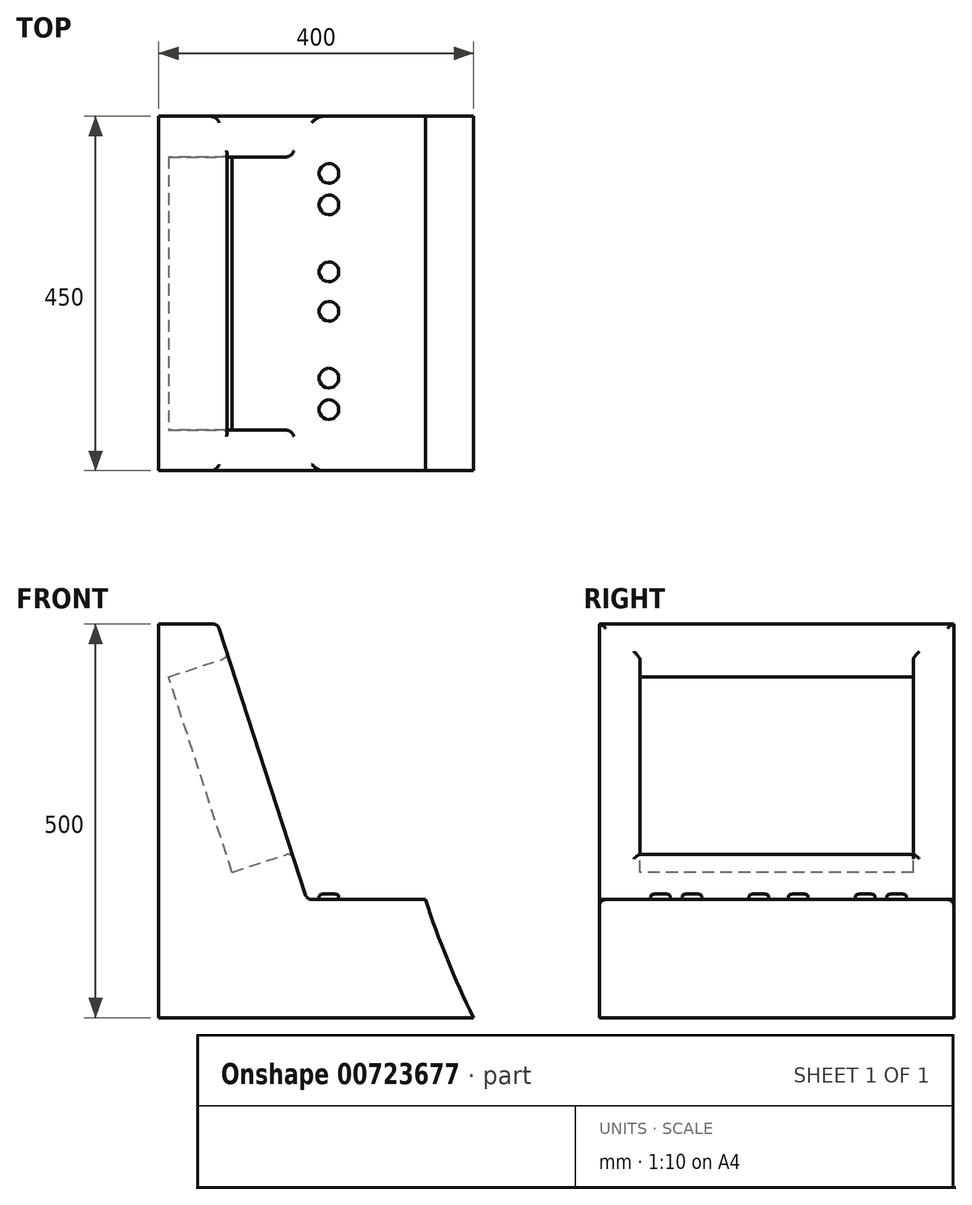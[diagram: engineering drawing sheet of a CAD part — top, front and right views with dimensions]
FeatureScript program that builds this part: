
annotation { "Feature Type Name" : "Feature", "Feature Type Description" : "" }
export const myFeature = defineFeature(function(context is Context, id is Id, definition is map)
    precondition{}
    {
        {
            var Q0;
            Q0=qCreatedBy(makeId("Front.planeOp"),FACE);
            var sketch = newSketch(context, id + "F0", { "sketchPlane" : qUnion([Q0])});
            skLineSegment(sketch, "E0", {"start": v(-195.47, 342.68) * mm, "end": v(-195.47, -157.32) * mm});
            skLineSegment(sketch, "E1", {"start": v(204.53, -157.32) * mm, "end": v(-195.47, -157.32) * mm});
            skLineSegment(sketch, "E2", {"start": v(143.25, -7.32) * mm, "end": v(-6.75, -7.32) * mm});
            skLineSegment(sketch, "E3", {"start": v(-195.47, 342.68) * mm, "end": v(-120.47, 342.68) * mm});
            skLineSegment(sketch, "E4", {"start": v(-120.47, 342.68) * mm, "end": v(-6.75, -7.32) * mm});
            skArc(sketch, "E5", {"start": v(143.25, -7.32) * mm, "mid": v(171.35, -83.36) * mm, "end": v(204.53, -157.32) * mm});
            skSolve(sketch);
        }
        {
            var Q0;
            Q0=makeQuery(id+"F0.imprint","IMPRINT",FACE,{"disambiguationData":[TD([[makeQuery(id+"F0.imprint","IMPRINT",EDGE,{"derivedFrom":sQuery(id+"F0.wireOp",EDGE,"E0")}),1.0]])]});
            extrude(context, id + "F1", {"entities" : qUnion([Q0]), "depth" : 450 * mm, "offsetDistance" : 25 * mm});
        }
        {
            var Q0;
            Q0=makeQuery(id+"F1.opExtrude","SWEPT_FACE",FACE,{"disambiguationData":[OSD([sQuery(id+"F0.wireOp",EDGE,"E4")])]});
            var sketch = newSketch(context, id + "F2", { "sketchPlane" : qUnion([Q0])});
            skLineSegment(sketch, "E6.bottom", {"start": v(-51.5, 57.64) * mm, "end": v(-398.5, 57.64) * mm});
            skLineSegment(sketch, "E6.top", {"start": v(-51.5, 318.64) * mm, "end": v(-398.5, 318.64) * mm});
            skLineSegment(sketch, "E6.left", {"start": v(-51.5, 57.64) * mm, "end": v(-51.5, 318.64) * mm});
            skLineSegment(sketch, "E6.right", {"start": v(-398.5, 57.64) * mm, "end": v(-398.5, 318.64) * mm});
            skPoint(sketch, "E6.middle", {"position": v(-225, 188.14) * mm});
            skSolve(sketch);
        }
        {
            var Q0;
            Q0=makeQuery(id+"F2.imprint","IMPRINT",FACE,{"disambiguationData":[TD([[makeQuery(id+"F2.imprint","IMPRINT",EDGE,{"derivedFrom":sQuery(id+"F2.wireOp",EDGE,"E6.bottom")}),-1.0]])]});
            extrude(context, id + "F3", {"entities" : qUnion([Q0]), "operationType" : NewBodyOperationType.REMOVE, "oppositeDirection" : true, "depth" : 80 * mm, "offsetDistance" : 25 * mm});
        }
        {
            var Q0;
            Q0=makeQuery(id+"F1.opExtrude","SWEPT_FACE",FACE,{"disambiguationData":[OSD([sQuery(id+"F0.wireOp",EDGE,"E4")])]});
            fillet(context, id + "F4", {"entities" : qUnion([Q0]), "radius" : 8 * mm, "tangentPropagation" : true, "allowEdgeOverflow" : false});
        }
        {
            var Q0;
            Q0=makeQuery(id+"F1.opExtrude","SWEPT_FACE",FACE,{"disambiguationData":[OSD([sQuery(id+"F0.wireOp",EDGE,"E2")])]});
            var sketch = newSketch(context, id + "F5", { "sketchPlane" : qUnion([Q0])});
            skLineSegment(sketch, "E7", {"start": v(20.89, -442) * mm, "end": v(20.89, -8) * mm, "construction": true});
            skCircle(sketch, "E8", {"center": v(20.89, -372.5) * mm, "radius": 12.5 * mm});
            skCircle(sketch, "E9", {"center": v(20.89, -332.5) * mm, "radius": 12.5 * mm});
            skCircle(sketch, "E10", {"center": v(20.89, -247.5) * mm, "radius": 12.5 * mm});
            skCircle(sketch, "E11", {"center": v(20.89, -197.5) * mm, "radius": 12.5 * mm});
            skCircle(sketch, "E12", {"center": v(20.89, -112.5) * mm, "radius": 12.5 * mm});
            skCircle(sketch, "E13", {"center": v(20.89, -72.5) * mm, "radius": 12.5 * mm});
            skSolve(sketch);
        }
        {
            var Q0;
            Q0=makeQuery(id+"F5.imprint","IMPRINT",FACE,{"disambiguationData":[TD([[makeQuery(id+"F5.imprint","IMPRINT",EDGE,{"derivedFrom":sQuery(id+"F5.wireOp",EDGE,"E8")}),1.0]])]});
            var Q1;
            Q1=makeQuery(id+"F5.imprint","IMPRINT",FACE,{"disambiguationData":[TD([[makeQuery(id+"F5.imprint","IMPRINT",EDGE,{"derivedFrom":sQuery(id+"F5.wireOp",EDGE,"E9")}),1.0]])]});
            var Q2;
            Q2=makeQuery(id+"F5.imprint","IMPRINT",FACE,{"disambiguationData":[TD([[makeQuery(id+"F5.imprint","IMPRINT",EDGE,{"derivedFrom":sQuery(id+"F5.wireOp",EDGE,"E10")}),1.0]])]});
            var Q3;
            Q3=makeQuery(id+"F5.imprint","IMPRINT",FACE,{"disambiguationData":[TD([[makeQuery(id+"F5.imprint","IMPRINT",EDGE,{"derivedFrom":sQuery(id+"F5.wireOp",EDGE,"E11")}),1.0]])]});
            var Q4;
            Q4=makeQuery(id+"F5.imprint","IMPRINT",FACE,{"disambiguationData":[TD([[makeQuery(id+"F5.imprint","IMPRINT",EDGE,{"derivedFrom":sQuery(id+"F5.wireOp",EDGE,"E12")}),1.0]])]});
            var Q5;
            Q5=makeQuery(id+"F5.imprint","IMPRINT",FACE,{"disambiguationData":[TD([[makeQuery(id+"F5.imprint","IMPRINT",EDGE,{"derivedFrom":sQuery(id+"F5.wireOp",EDGE,"E13")}),1.0]])]});
            extrude(context, id + "F6", {"entities" : qUnion([Q0, Q1, Q2, Q3, Q4, Q5]), "operationType" : NewBodyOperationType.ADD, "depth" : 7 * mm, "offsetDistance" : 25 * mm});
        }
        {
            var Q0;
            Q0=makeQuery(id+"F6.opExtrude","CAP_FACE",FACE,{"disambiguationData":[OSD([sQuery(id+"F5.wireOp",EDGE,"E8")])],"isStart":false});
            fillet(context, id + "F7", {"entities" : qUnion([Q0]), "radius" : 7 * mm, "tangentPropagation" : true, "rho" : 0.7, "crossSection" : FilletCrossSection.CONIC, "allowEdgeOverflow" : false});
        }
        {
            var Q0;
            Q0=makeQuery(id+"F6.opExtrude","CAP_FACE",FACE,{"disambiguationData":[OSD([sQuery(id+"F5.wireOp",EDGE,"E9")])],"isStart":false});
            var Q1;
            Q1=makeQuery(id+"F6.opExtrude","CAP_FACE",FACE,{"disambiguationData":[OSD([sQuery(id+"F5.wireOp",EDGE,"E11")])],"isStart":false});
            var Q2;
            Q2=makeQuery(id+"F6.opExtrude","CAP_FACE",FACE,{"disambiguationData":[OSD([sQuery(id+"F5.wireOp",EDGE,"E10")])],"isStart":false});
            var Q3;
            Q3=makeQuery(id+"F6.opExtrude","CAP_FACE",FACE,{"disambiguationData":[OSD([sQuery(id+"F5.wireOp",EDGE,"E12")])],"isStart":false});
            var Q4;
            Q4=makeQuery(id+"F6.opExtrude","CAP_FACE",FACE,{"disambiguationData":[OSD([sQuery(id+"F5.wireOp",EDGE,"E13")])],"isStart":false});
            fillet(context, id + "F8", {"entities" : qUnion([Q0, Q1, Q2, Q3, Q4]), "radius" : 7 * mm, "tangentPropagation" : true, "rho" : 0.7, "crossSection" : FilletCrossSection.CONIC, "allowEdgeOverflow" : false});
        }
    });
